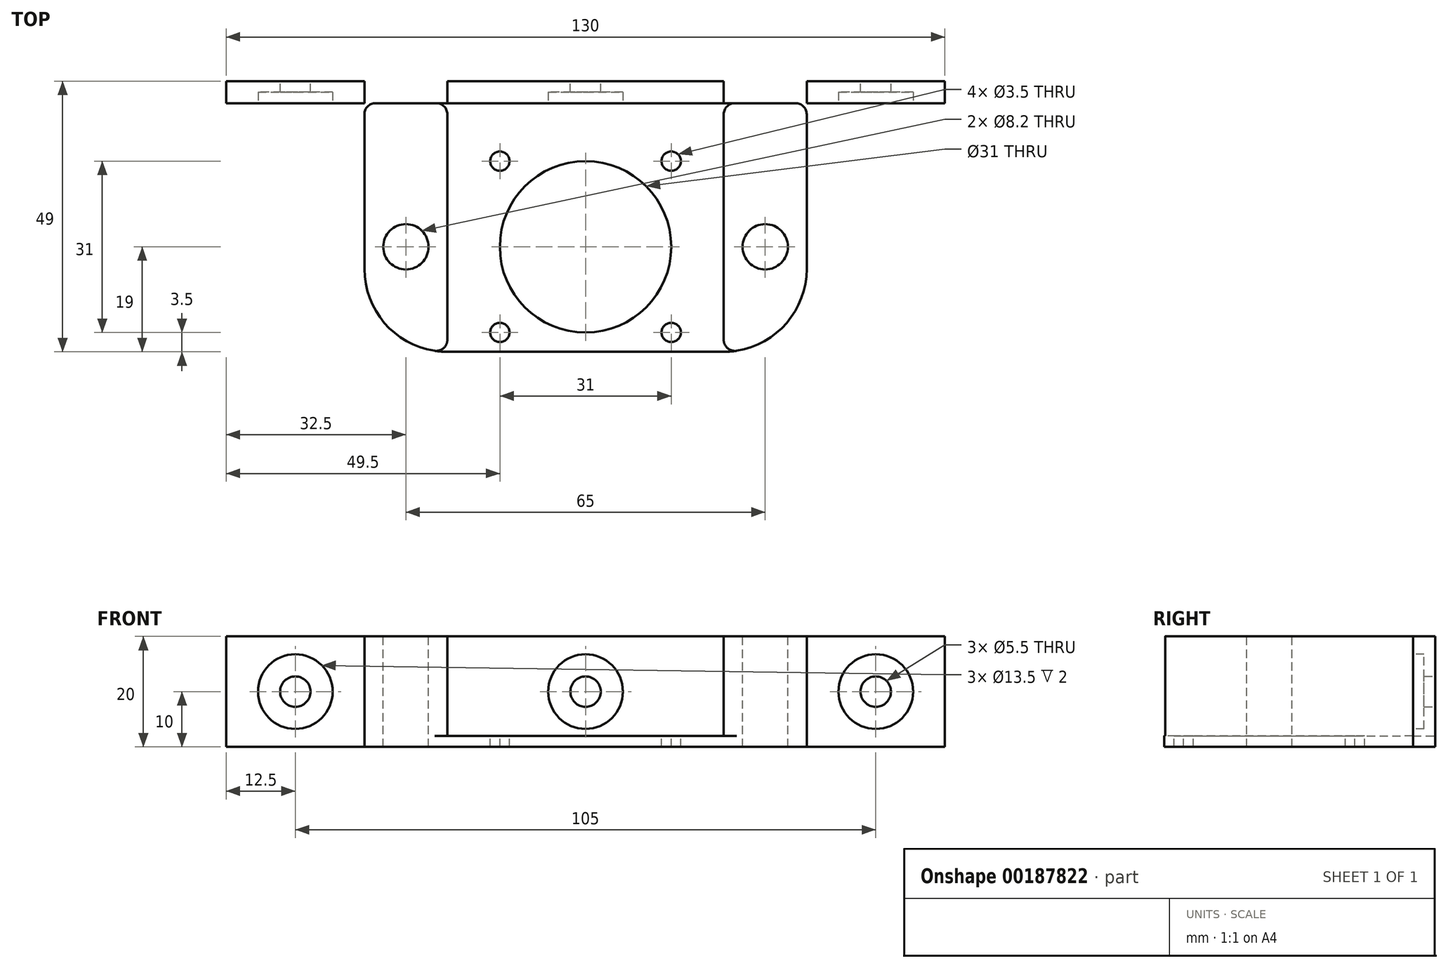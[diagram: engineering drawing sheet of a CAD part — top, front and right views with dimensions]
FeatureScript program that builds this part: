
annotation { "Feature Type Name" : "Feature", "Feature Type Description" : "" }
export const myFeature = defineFeature(function(context is Context, id is Id, definition is map)
    precondition{}
    {
        {
            var Q0;
            Q0=qCreatedBy(makeId("Front.planeOp"),FACE);
            var sketch = newSketch(context, id + "F0", { "sketchPlane" : qUnion([Q0])});
            skLineSegment(sketch, "E0.bottom", {"start": v(0, 0) * mm, "end": v(130, 0) * mm});
            skLineSegment(sketch, "E0.left", {"start": v(0, 0) * mm, "end": v(0, 20) * mm});
            skLineSegment(sketch, "E0.right", {"start": v(130, 0) * mm, "end": v(130, 20) * mm});
            skLineSegment(sketch, "E1.bottom", {"start": v(40, 20) * mm, "end": v(90, 20) * mm});
            skLineSegment(sketch, "E1.top", {"start": v(40, 0) * mm, "end": v(90, 0) * mm});
            skLineSegment(sketch, "E1.left", {"start": v(40, 20) * mm, "end": v(40, 0) * mm});
            skLineSegment(sketch, "E1.right", {"start": v(90, 20) * mm, "end": v(90, 0) * mm});
            skLineSegment(sketch, "E2", {"start": v(0, 20) * mm, "end": v(40, 20) * mm});
            skLineSegment(sketch, "E3", {"start": v(90, 20) * mm, "end": v(130, 20) * mm});
            skLineSegment(sketch, "E4.bottom", {"start": v(40, 20) * mm, "end": v(25, 20) * mm});
            skLineSegment(sketch, "E4.top", {"start": v(40, 0) * mm, "end": v(25, 0) * mm});
            skLineSegment(sketch, "E4.right", {"start": v(25, 20) * mm, "end": v(25, 0) * mm});
            skLineSegment(sketch, "E5.bottom", {"start": v(90, 20) * mm, "end": v(105, 20) * mm});
            skLineSegment(sketch, "E5.top", {"start": v(90, 0) * mm, "end": v(105, 0) * mm});
            skLineSegment(sketch, "E5.right", {"start": v(105, 20) * mm, "end": v(105, 0) * mm});
            skCircle(sketch, "E6", {"center": v(12.5, 10) * mm, "radius": 2.75 * mm});
            skCircle(sketch, "E7", {"center": v(117.5, 10) * mm, "radius": 2.75 * mm});
            skLineSegment(sketch, "E8.top", {"start": v(40, 2) * mm, "end": v(90, 2) * mm});
            skLineSegment(sketch, "E8.left", {"start": v(40, 0) * mm, "end": v(40, 2) * mm});
            skLineSegment(sketch, "E8.right", {"start": v(90, 0) * mm, "end": v(90, 2) * mm});
            skLineSegment(sketch, "E9", {"start": v(0, 10) * mm, "end": v(12.5, 10) * mm});
            skLineSegment(sketch, "E10", {"start": v(12.5, 10) * mm, "end": v(65, 10) * mm});
            skLineSegment(sketch, "E11", {"start": v(117.5, 10) * mm, "end": v(65, 10) * mm});
            skLineSegment(sketch, "E12", {"start": v(117.5, 10) * mm, "end": v(130, 10) * mm});
            skCircle(sketch, "E13", {"center": v(12.5, 10) * mm, "radius": 6.75 * mm});
            skCircle(sketch, "E14", {"center": v(117.5, 10) * mm, "radius": 6.75 * mm});
            skCircle(sketch, "E15", {"center": v(65, 10) * mm, "radius": 2.75 * mm});
            skCircle(sketch, "E16", {"center": v(65.03, 10.1) * mm, "radius": 6.75 * mm});
            skSolve(sketch);
        }
        {
            var Q0;
            {var subQ1=sQuery(id+"F0.wireOp",EDGE,"E0.left");Q0=makeQuery(id+"F0.imprint","IMPRINT",FACE,{"disambiguationData":[TD([[makeQuery(id+"F0.imprint","IMPRINT",EDGE,{"derivedFrom":subQ1}),-1.0]])]});}
            var Q1;
            {var subQ1=sQuery(id+"F0.wireOp",EDGE,"E0.right");Q1=makeQuery(id+"F0.imprint","IMPRINT",FACE,{"disambiguationData":[TD([[makeQuery(id+"F0.imprint","IMPRINT",EDGE,{"derivedFrom":subQ1}),1.0]])]});}
            var Q2;
            Q2=makeQuery(id+"F0.imprint","IMPRINT",FACE,{"disambiguationData":[TD([[makeQuery(id+"F0.imprint","IMPRINT",EDGE,{"derivedFrom":sQuery(id+"F0.wireOp",EDGE,"E1.bottom")}),-1.0]])]});
            var Q3;
            Q3=makeQuery(id+"F0.imprint","IMPRINT",FACE,{"disambiguationData":[TD([[makeQuery(id+"F0.imprint","IMPRINT",EDGE,{"derivedFrom":sQuery(id+"F0.wireOp",EDGE,"E4.bottom")}),1.0]])]});
            var Q4;
            Q4=makeQuery(id+"F0.imprint","IMPRINT",FACE,{"disambiguationData":[TD([[makeQuery(id+"F0.imprint","IMPRINT",EDGE,{"derivedFrom":sQuery(id+"F0.wireOp",EDGE,"E5.bottom")}),-1.0]])]});
            var Q5;
            Q5=makeQuery(id+"F0.imprint","IMPRINT",FACE,{"disambiguationData":[TD([[makeQuery(id+"F0.imprint","IMPRINT",EDGE,{"derivedFrom":sQuery(id+"F0.wireOp",EDGE,"E1.top")}),1.0]])]});
            var Q6;
            {var subQ6=sQuery(id+"F0.wireOp",EDGE,"E4.top");Q6=makeQuery(id+"F0.imprint","IMPRINT",FACE,{"disambiguationData":[TD([[makeQuery(id+"F0.imprint","IMPRINT",EDGE,{"derivedFrom":subQ6}),-1.0]])]});}
            var Q7;
            {var subQ9=sQuery(id+"F0.wireOp",EDGE,"E8.top");Q7=makeQuery(id+"F0.imprint","IMPRINT",FACE,{"disambiguationData":[TD([[makeQuery(id+"F0.imprint","IMPRINT",EDGE,{"derivedFrom":subQ9}),1.0]])]});}
            var Q8;
            {var subQ6=sQuery(id+"F0.wireOp",EDGE,"E5.top");Q8=makeQuery(id+"F0.imprint","IMPRINT",FACE,{"disambiguationData":[TD([[makeQuery(id+"F0.imprint","IMPRINT",EDGE,{"derivedFrom":subQ6}),1.0]])]});}
            var Q9;
            {var subQ3=sQuery(id+"F0.wireOp",EDGE,"E9");var subQ5=sQuery(id+"F0.wireOp",EDGE,"E6");var subQ7=makeQuery(id+"F0.imprint","INTERSECT",VERTEX,{"derivedFrom":[subQ5,subQ3]});Q9=makeQuery(id+"F0.imprint","IMPRINT",FACE,{"disambiguationData":[TD([[makeQuery(id+"F0.imprint","IMPRINT",EDGE,{"disambiguationData":[TD([[subQ7,1.0]])],"derivedFrom":subQ5}),-1.0]])]});}
            var Q10;
            {var subQ3=sQuery(id+"F0.wireOp",EDGE,"E9");var subQ5=sQuery(id+"F0.wireOp",EDGE,"E6");var subQ7=makeQuery(id+"F0.imprint","INTERSECT",VERTEX,{"derivedFrom":[subQ5,subQ3]});Q10=makeQuery(id+"F0.imprint","IMPRINT",FACE,{"disambiguationData":[TD([[makeQuery(id+"F0.imprint","IMPRINT",EDGE,{"disambiguationData":[TD([[subQ7,-1.0]])],"derivedFrom":subQ5}),-1.0]])]});}
            var Q11;
            {var subQ0=sQuery(id+"F0.wireOp",EDGE,"E16");var subQ3=sQuery(id+"F0.wireOp",EDGE,"E10");var subQ4=makeQuery(id+"F0.imprint","INTERSECT",VERTEX,{"derivedFrom":[subQ3,subQ0]});Q11=makeQuery(id+"F0.imprint","IMPRINT",FACE,{"disambiguationData":[TD([[makeQuery(id+"F0.imprint","IMPRINT",EDGE,{"disambiguationData":[TD([[subQ4,-1.0]])],"derivedFrom":subQ3}),-1.0]])]});}
            var Q12;
            {var subQ0=sQuery(id+"F0.wireOp",EDGE,"E16");var subQ3=sQuery(id+"F0.wireOp",EDGE,"E10");var subQ4=makeQuery(id+"F0.imprint","INTERSECT",VERTEX,{"derivedFrom":[subQ3,subQ0]});Q12=makeQuery(id+"F0.imprint","IMPRINT",FACE,{"disambiguationData":[TD([[makeQuery(id+"F0.imprint","IMPRINT",EDGE,{"disambiguationData":[TD([[subQ4,-1.0]])],"derivedFrom":subQ3}),1.0]])]});}
            var Q13;
            {var subQ3=sQuery(id+"F0.wireOp",EDGE,"E11");var subQ5=sQuery(id+"F0.wireOp",EDGE,"E7");var subQ7=makeQuery(id+"F0.imprint","INTERSECT",VERTEX,{"derivedFrom":[subQ5,subQ3]});Q13=makeQuery(id+"F0.imprint","IMPRINT",FACE,{"disambiguationData":[TD([[makeQuery(id+"F0.imprint","IMPRINT",EDGE,{"disambiguationData":[TD([[subQ7,1.0]])],"derivedFrom":subQ5}),-1.0]])]});}
            var Q14;
            {var subQ3=sQuery(id+"F0.wireOp",EDGE,"E11");var subQ5=sQuery(id+"F0.wireOp",EDGE,"E7");var subQ7=makeQuery(id+"F0.imprint","INTERSECT",VERTEX,{"derivedFrom":[subQ5,subQ3]});Q14=makeQuery(id+"F0.imprint","IMPRINT",FACE,{"disambiguationData":[TD([[makeQuery(id+"F0.imprint","IMPRINT",EDGE,{"disambiguationData":[TD([[subQ7,-1.0]])],"derivedFrom":subQ5}),-1.0]])]});}
            extrude(context, id + "F1", {"entities" : qUnion([Q0, Q1, Q2, Q3, Q4, Q5, Q6, Q7, Q8, Q9, Q10, Q11, Q12, Q13, Q14]), "depth" : 4 * mm});
        }
        {
            var Q0;
            Q0=makeQuery(id+"F1.opExtrude","CAP_FACE",FACE,{"disambiguationData":[OSD([sQuery(id+"F0.wireOp",EDGE,"E0.bottom"),sQuery(id+"F0.wireOp",EDGE,"E0.left"),sQuery(id+"F0.wireOp",EDGE,"E0.right"),sQuery(id+"F0.wireOp",EDGE,"E1.bottom"),sQuery(id+"F0.wireOp",EDGE,"E2"),sQuery(id+"F0.wireOp",EDGE,"E3"),sQuery(id+"F0.wireOp",EDGE,"E4.bottom"),sQuery(id+"F0.wireOp",EDGE,"E4.top"),sQuery(id+"F0.wireOp",EDGE,"E5.bottom"),sQuery(id+"F0.wireOp",EDGE,"E5.top"),sQuery(id+"F0.wireOp",EDGE,"E6"),sQuery(id+"F0.wireOp",EDGE,"E7"),sQuery(id+"F0.wireOp",EDGE,"E1.top"),sQuery(id+"F0.wireOp",EDGE,"E15")])],"isStart":false});
            var sketch = newSketch(context, id + "F2", { "sketchPlane" : qUnion([Q0])});
            skCircle(sketch, "E17", {"center": v(12.5, 10) * mm, "radius": 6.75 * mm});
            skCircle(sketch, "E18", {"center": v(65, 10) * mm, "radius": 6.75 * mm});
            skCircle(sketch, "E19", {"center": v(117.5, 10) * mm, "radius": 6.75 * mm});
            skSolve(sketch);
        }
        {
            var Q0;
            Q0=qSketchRegion(id+"F2",true);
            extrude(context, id + "F3", {"entities" : qUnion([Q0]), "operationType" : NewBodyOperationType.REMOVE, "oppositeDirection" : true, "depth" : 2 * mm});
        }
        {
            var Q0;
            Q0=makeQuery(id+"F1.opExtrude","CAP_FACE",FACE,{"disambiguationData":[OSD([sQuery(id+"F0.wireOp",EDGE,"E0.bottom"),sQuery(id+"F0.wireOp",EDGE,"E0.left"),sQuery(id+"F0.wireOp",EDGE,"E0.right"),sQuery(id+"F0.wireOp",EDGE,"E1.bottom"),sQuery(id+"F0.wireOp",EDGE,"E2"),sQuery(id+"F0.wireOp",EDGE,"E3"),sQuery(id+"F0.wireOp",EDGE,"E4.bottom"),sQuery(id+"F0.wireOp",EDGE,"E4.top"),sQuery(id+"F0.wireOp",EDGE,"E5.bottom"),sQuery(id+"F0.wireOp",EDGE,"E5.top"),sQuery(id+"F0.wireOp",EDGE,"E6"),sQuery(id+"F0.wireOp",EDGE,"E7"),sQuery(id+"F0.wireOp",EDGE,"E1.top")])],"isStart":false});
            var sketch = newSketch(context, id + "F4", { "sketchPlane" : qUnion([Q0])});
            skLineSegment(sketch, "E20.bottom", {"start": v(25, 20) * mm, "end": v(40, 20) * mm});
            skLineSegment(sketch, "E20.top", {"start": v(25, 0) * mm, "end": v(40, 0) * mm});
            skLineSegment(sketch, "E20.left", {"start": v(25, 20) * mm, "end": v(25, 0) * mm});
            skLineSegment(sketch, "E20.right", {"start": v(40, 20) * mm, "end": v(40, 0) * mm});
            skLineSegment(sketch, "E21.bottom", {"start": v(90, 20) * mm, "end": v(105, 20) * mm});
            skLineSegment(sketch, "E21.top", {"start": v(90, 0) * mm, "end": v(105, 0) * mm});
            skLineSegment(sketch, "E21.left", {"start": v(90, 20) * mm, "end": v(90, 0) * mm});
            skLineSegment(sketch, "E21.right", {"start": v(105, 20) * mm, "end": v(105, 0) * mm});
            skLineSegment(sketch, "E22", {"start": v(0, 20) * mm, "end": v(25, 20) * mm});
            skLineSegment(sketch, "E23", {"start": v(105, 20) * mm, "end": v(130, 20) * mm});
            skLineSegment(sketch, "E24.bottom", {"start": v(40, 0) * mm, "end": v(90, 0) * mm});
            skLineSegment(sketch, "E24.top", {"start": v(40, 0) * mm, "end": v(90, 0) * mm});
            skLineSegment(sketch, "E24.left", {"start": v(40, 0) * mm, "end": v(40, 0) * mm});
            skLineSegment(sketch, "E24.right", {"start": v(90, 0) * mm, "end": v(90, 0) * mm});
            skLineSegment(sketch, "E25.bottom", {"start": v(90, 0) * mm, "end": v(40, 0) * mm});
            skLineSegment(sketch, "E25.top", {"start": v(90, 2) * mm, "end": v(40, 2) * mm});
            skLineSegment(sketch, "E25.left", {"start": v(90, 0) * mm, "end": v(90, 2) * mm});
            skLineSegment(sketch, "E25.right", {"start": v(40, 0) * mm, "end": v(40, 2) * mm});
            skSolve(sketch);
        }
        {
            var Q0;
            Q0=qSketchRegion(id+"F4",true);
            extrude(context, id + "F5", {"entities" : qUnion([Q0]), "operationType" : NewBodyOperationType.ADD, "depth" : 45 * mm});
        }
        {
            var Q0;
            Q0=makeQuery(id+"F5.opExtrude","SWEPT_FACE",FACE,{"disambiguationData":[OSD([sQuery(id+"F4.wireOp",EDGE,"E25.top")])]});
            var sketch = newSketch(context, id + "F6", { "sketchPlane" : qUnion([Q0])});
            skLineSegment(sketch, "E26.bottom", {"start": v(43.85, -8.85) * mm, "end": v(86.15, -8.85) * mm});
            skLineSegment(sketch, "E26.top", {"start": v(43.85, -51.15) * mm, "end": v(86.15, -51.15) * mm});
            skLineSegment(sketch, "E26.left", {"start": v(43.85, -8.85) * mm, "end": v(43.85, -51.15) * mm});
            skLineSegment(sketch, "E26.right", {"start": v(86.15, -8.85) * mm, "end": v(86.15, -51.15) * mm});
            skLineSegment(sketch, "E27.bottom", {"start": v(49.5, -14.5) * mm, "end": v(80.5, -14.5) * mm});
            skLineSegment(sketch, "E27.top", {"start": v(49.5, -45.5) * mm, "end": v(80.5, -45.5) * mm});
            skLineSegment(sketch, "E27.left", {"start": v(49.5, -14.5) * mm, "end": v(49.5, -45.5) * mm});
            skLineSegment(sketch, "E27.right", {"start": v(80.5, -14.5) * mm, "end": v(80.5, -45.5) * mm});
            skLineSegment(sketch, "E28", {"start": v(43.85, -51.15) * mm, "end": v(49.5, -45.5) * mm});
            skLineSegment(sketch, "E29", {"start": v(80.5, -14.5) * mm, "end": v(86.15, -8.85) * mm});
            skCircle(sketch, "E30", {"center": v(49.5, -14.5) * mm, "radius": 1.75 * mm});
            skCircle(sketch, "E31", {"center": v(49.5, -45.5) * mm, "radius": 1.75 * mm});
            skCircle(sketch, "E32", {"center": v(80.5, -45.5) * mm, "radius": 1.75 * mm});
            skCircle(sketch, "E33", {"center": v(80.5, -14.5) * mm, "radius": 1.75 * mm});
            skLineSegment(sketch, "E34", {"start": v(65, -30) * mm, "end": v(65, 0) * mm});
            skLineSegment(sketch, "E35", {"start": v(43.85, -51.15) * mm, "end": v(40, -51.15) * mm});
            skLineSegment(sketch, "E36", {"start": v(86.15, -51.15) * mm, "end": v(90, -51.15) * mm});
            skLineSegment(sketch, "E37", {"start": v(49.5, -45.5) * mm, "end": v(65, -30) * mm});
            skLineSegment(sketch, "E38", {"start": v(65, -30) * mm, "end": v(80.5, -14.5) * mm});
            skCircle(sketch, "E39", {"center": v(65, -30) * mm, "radius": 15.5 * mm});
            skSolve(sketch);
        }
        {
            var Q0;
            {var subQ0=sQuery(id+"F6.wireOp",EDGE,"E31");var subQ3=sQuery(id+"F6.wireOp",EDGE,"E27.top");var subQ4=makeQuery(id+"F6.imprint","INTERSECT",VERTEX,{"derivedFrom":[subQ3,subQ0]});Q0=makeQuery(id+"F6.imprint","IMPRINT",FACE,{"disambiguationData":[TD([[makeQuery(id+"F6.imprint","IMPRINT",EDGE,{"disambiguationData":[TD([[subQ4,1.0]])],"derivedFrom":subQ0}),1.0]])]});}
            var Q1;
            {var subQ0=sQuery(id+"F6.wireOp",EDGE,"E31");var subQ3=sQuery(id+"F6.wireOp",EDGE,"E27.left");var subQ4=makeQuery(id+"F6.imprint","INTERSECT",VERTEX,{"derivedFrom":[subQ3,subQ0]});Q1=makeQuery(id+"F6.imprint","IMPRINT",FACE,{"disambiguationData":[TD([[makeQuery(id+"F6.imprint","IMPRINT",EDGE,{"disambiguationData":[TD([[subQ4,-1.0]])],"derivedFrom":subQ0}),1.0]])]});}
            var Q2;
            {var subQ1=sQuery(id+"F6.wireOp",EDGE,"E27.left");var subQ3=sQuery(id+"F6.wireOp",EDGE,"E27.bottom");var subQ5=makeQuery(id+"F6.imprint","INTERSECT",VERTEX,{"derivedFrom":[subQ3,subQ1]});Q2=makeQuery(id+"F6.imprint","IMPRINT",FACE,{"disambiguationData":[TD([[makeQuery(id+"F6.imprint","IMPRINT",EDGE,{"disambiguationData":[TD([[subQ5,-1.0]])],"derivedFrom":subQ3}),-1.0]])]});}
            var Q3;
            {var subQ1=sQuery(id+"F6.wireOp",EDGE,"E27.left");var subQ3=sQuery(id+"F6.wireOp",EDGE,"E27.bottom");var subQ5=makeQuery(id+"F6.imprint","INTERSECT",VERTEX,{"derivedFrom":[subQ3,subQ1]});Q3=makeQuery(id+"F6.imprint","IMPRINT",FACE,{"disambiguationData":[TD([[makeQuery(id+"F6.imprint","IMPRINT",EDGE,{"disambiguationData":[TD([[subQ5,-1.0]])],"derivedFrom":subQ3}),1.0]])]});}
            var Q4;
            {var subQ0=sQuery(id+"F6.wireOp",EDGE,"E33");var subQ3=sQuery(id+"F6.wireOp",EDGE,"E27.bottom");var subQ4=makeQuery(id+"F6.imprint","INTERSECT",VERTEX,{"derivedFrom":[subQ3,subQ0]});Q4=makeQuery(id+"F6.imprint","IMPRINT",FACE,{"disambiguationData":[TD([[makeQuery(id+"F6.imprint","IMPRINT",EDGE,{"disambiguationData":[TD([[subQ4,1.0]])],"derivedFrom":subQ0}),1.0]])]});}
            var Q5;
            {var subQ0=sQuery(id+"F6.wireOp",EDGE,"E33");var subQ3=sQuery(id+"F6.wireOp",EDGE,"E27.bottom");var subQ4=makeQuery(id+"F6.imprint","INTERSECT",VERTEX,{"derivedFrom":[subQ3,subQ0]});Q5=makeQuery(id+"F6.imprint","IMPRINT",FACE,{"disambiguationData":[TD([[makeQuery(id+"F6.imprint","IMPRINT",EDGE,{"disambiguationData":[TD([[subQ4,-1.0]])],"derivedFrom":subQ0}),1.0]])]});}
            var Q6;
            {var subQ0=sQuery(id+"F6.wireOp",EDGE,"E33");var subQ3=sQuery(id+"F6.wireOp",EDGE,"E27.right");var subQ4=makeQuery(id+"F6.imprint","INTERSECT",VERTEX,{"derivedFrom":[subQ3,subQ0]});Q6=makeQuery(id+"F6.imprint","IMPRINT",FACE,{"disambiguationData":[TD([[makeQuery(id+"F6.imprint","IMPRINT",EDGE,{"disambiguationData":[TD([[subQ4,-1.0]])],"derivedFrom":subQ0}),1.0]])]});}
            var Q7;
            {var subQ1=sQuery(id+"F6.wireOp",EDGE,"E27.right");var subQ3=sQuery(id+"F6.wireOp",EDGE,"E27.top");var subQ5=makeQuery(id+"F6.imprint","INTERSECT",VERTEX,{"derivedFrom":[subQ3,subQ1]});Q7=makeQuery(id+"F6.imprint","IMPRINT",FACE,{"disambiguationData":[TD([[makeQuery(id+"F6.imprint","IMPRINT",EDGE,{"disambiguationData":[TD([[subQ5,1.0]])],"derivedFrom":subQ3}),-1.0]])]});}
            var Q8;
            {var subQ1=sQuery(id+"F6.wireOp",EDGE,"E27.right");var subQ3=sQuery(id+"F6.wireOp",EDGE,"E27.top");var subQ5=makeQuery(id+"F6.imprint","INTERSECT",VERTEX,{"derivedFrom":[subQ3,subQ1]});Q8=makeQuery(id+"F6.imprint","IMPRINT",FACE,{"disambiguationData":[TD([[makeQuery(id+"F6.imprint","IMPRINT",EDGE,{"disambiguationData":[TD([[subQ5,1.0]])],"derivedFrom":subQ3}),1.0]])]});}
            var Q9;
            {var subQ1=sQuery(id+"F6.wireOp",EDGE,"E33");var subQ3=sQuery(id+"F6.wireOp",EDGE,"E27.right");var subQ5=makeQuery(id+"F6.imprint","INTERSECT",VERTEX,{"derivedFrom":[subQ3,subQ1]});Q9=makeQuery(id+"F6.imprint","IMPRINT",FACE,{"disambiguationData":[TD([[makeQuery(id+"F6.imprint","IMPRINT",EDGE,{"disambiguationData":[TD([[subQ5,1.0]])],"derivedFrom":subQ1}),1.0]])]});}
            var Q10;
            {var subQ1=sQuery(id+"F6.wireOp",EDGE,"E31");var subQ3=sQuery(id+"F6.wireOp",EDGE,"E27.top");var subQ5=makeQuery(id+"F6.imprint","INTERSECT",VERTEX,{"derivedFrom":[subQ3,subQ1]});Q10=makeQuery(id+"F6.imprint","IMPRINT",FACE,{"disambiguationData":[TD([[makeQuery(id+"F6.imprint","IMPRINT",EDGE,{"disambiguationData":[TD([[subQ5,-1.0]])],"derivedFrom":subQ1}),1.0]])]});}
            var Q11;
            {var subQ1=sQuery(id+"F6.wireOp",EDGE,"E31");var subQ3=sQuery(id+"F6.wireOp",EDGE,"E27.left");var subQ5=makeQuery(id+"F6.imprint","INTERSECT",VERTEX,{"derivedFrom":[subQ3,subQ1]});Q11=makeQuery(id+"F6.imprint","IMPRINT",FACE,{"disambiguationData":[TD([[makeQuery(id+"F6.imprint","IMPRINT",EDGE,{"disambiguationData":[TD([[subQ5,1.0]])],"derivedFrom":subQ1}),1.0]])]});}
            var Q12;
            {var subQ0=sQuery(id+"F6.wireOp",EDGE,"E39");var subQ3=sQuery(id+"F6.wireOp",EDGE,"E34");var subQ4=makeQuery(id+"F6.imprint","INTERSECT",VERTEX,{"derivedFrom":[subQ3,subQ0]});Q12=makeQuery(id+"F6.imprint","IMPRINT",FACE,{"disambiguationData":[TD([[makeQuery(id+"F6.imprint","IMPRINT",EDGE,{"disambiguationData":[TD([[subQ4,-1.0]])],"derivedFrom":subQ0}),1.0]])]});}
            var Q13;
            {var subQ0=sQuery(id+"F6.wireOp",EDGE,"E39");var subQ3=sQuery(id+"F6.wireOp",EDGE,"E34");var subQ4=makeQuery(id+"F6.imprint","INTERSECT",VERTEX,{"derivedFrom":[subQ3,subQ0]});Q13=makeQuery(id+"F6.imprint","IMPRINT",FACE,{"disambiguationData":[TD([[makeQuery(id+"F6.imprint","IMPRINT",EDGE,{"disambiguationData":[TD([[subQ4,1.0]])],"derivedFrom":subQ0}),1.0]])]});}
            var Q14;
            {var subQ0=sQuery(id+"F6.wireOp",EDGE,"E39");var subQ3=sQuery(id+"F6.wireOp",EDGE,"E37");var subQ4=makeQuery(id+"F6.imprint","INTERSECT",VERTEX,{"derivedFrom":[subQ3,subQ0]});Q14=makeQuery(id+"F6.imprint","IMPRINT",FACE,{"disambiguationData":[TD([[makeQuery(id+"F6.imprint","IMPRINT",EDGE,{"disambiguationData":[TD([[subQ4,-1.0]])],"derivedFrom":subQ0}),1.0]])]});}
            extrude(context, id + "F7", {"entities" : qUnion([Q0, Q1, Q2, Q3, Q4, Q5, Q6, Q7, Q8, Q9, Q10, Q11, Q12, Q13, Q14]), "operationType" : NewBodyOperationType.REMOVE, "oppositeDirection" : true, "depth" : 2 * mm});
        }
        {
            var Q0;
            Q0=makeQuery(id+"F5.boolean.opBoolean","MERGE",FACE,{"derivedFrom":[makeQuery(id+"F1.opExtrude","SWEPT_FACE",FACE,{"disambiguationData":[OSD([sQuery(id+"F0.wireOp",EDGE,"E1.bottom"),sQuery(id+"F0.wireOp",EDGE,"E2"),sQuery(id+"F0.wireOp",EDGE,"E3"),sQuery(id+"F0.wireOp",EDGE,"E4.bottom"),sQuery(id+"F0.wireOp",EDGE,"E5.bottom")])]}),makeQuery(id+"F5.opExtrude","SWEPT_FACE",FACE,{"disambiguationData":[OSD([sQuery(id+"F4.wireOp",EDGE,"E20.bottom")])]}),makeQuery(id+"F5.opExtrude","SWEPT_FACE",FACE,{"disambiguationData":[OSD([sQuery(id+"F4.wireOp",EDGE,"E21.bottom")])]})]});
            var sketch = newSketch(context, id + "F8", { "sketchPlane" : qUnion([Q0])});
            skCircle(sketch, "E40", {"center": v(32.5, -30) * mm, "radius": 4.1 * mm});
            skCircle(sketch, "E41", {"center": v(97.5, -30) * mm, "radius": 4.1 * mm});
            skLineSegment(sketch, "E42", {"start": v(32.5, -30) * mm, "end": v(32.5, 0) * mm});
            skLineSegment(sketch, "E43", {"start": v(97.5, -30) * mm, "end": v(97.5, 0) * mm});
            skLineSegment(sketch, "E44", {"start": v(32.5, -30) * mm, "end": v(97.5, -30) * mm});
            skLineSegment(sketch, "E45", {"start": v(32.5, 0) * mm, "end": v(0, 0) * mm});
            skLineSegment(sketch, "E46", {"start": v(97.5, 0) * mm, "end": v(130, 0) * mm});
            skSolve(sketch);
        }
        {
            var Q0;
            {var subQ1=sQuery(id+"F8.wireOp",EDGE,"E40");var subQ3=sQuery(id+"F8.wireOp",EDGE,"E42");var subQ5=makeQuery(id+"F8.imprint","INTERSECT",VERTEX,{"derivedFrom":[subQ1,subQ3]});Q0=makeQuery(id+"F8.imprint","IMPRINT",FACE,{"disambiguationData":[TD([[makeQuery(id+"F8.imprint","IMPRINT",EDGE,{"disambiguationData":[TD([[subQ5,-1.0]])],"derivedFrom":subQ1}),1.0]])]});}
            var Q1;
            {var subQ1=sQuery(id+"F8.wireOp",EDGE,"E40");var subQ3=sQuery(id+"F8.wireOp",EDGE,"E42");var subQ5=makeQuery(id+"F8.imprint","INTERSECT",VERTEX,{"derivedFrom":[subQ1,subQ3]});Q1=makeQuery(id+"F8.imprint","IMPRINT",FACE,{"disambiguationData":[TD([[makeQuery(id+"F8.imprint","IMPRINT",EDGE,{"disambiguationData":[TD([[subQ5,1.0]])],"derivedFrom":subQ1}),1.0]])]});}
            var Q2;
            {var subQ1=sQuery(id+"F8.wireOp",EDGE,"E41");var subQ3=sQuery(id+"F8.wireOp",EDGE,"E43");var subQ5=makeQuery(id+"F8.imprint","INTERSECT",VERTEX,{"derivedFrom":[subQ1,subQ3]});Q2=makeQuery(id+"F8.imprint","IMPRINT",FACE,{"disambiguationData":[TD([[makeQuery(id+"F8.imprint","IMPRINT",EDGE,{"disambiguationData":[TD([[subQ5,-1.0]])],"derivedFrom":subQ1}),1.0]])]});}
            var Q3;
            {var subQ1=sQuery(id+"F8.wireOp",EDGE,"E41");var subQ3=sQuery(id+"F8.wireOp",EDGE,"E43");var subQ5=makeQuery(id+"F8.imprint","INTERSECT",VERTEX,{"derivedFrom":[subQ1,subQ3]});Q3=makeQuery(id+"F8.imprint","IMPRINT",FACE,{"disambiguationData":[TD([[makeQuery(id+"F8.imprint","IMPRINT",EDGE,{"disambiguationData":[TD([[subQ5,1.0]])],"derivedFrom":subQ1}),1.0]])]});}
            extrude(context, id + "F9", {"entities" : qUnion([Q0, Q1, Q2, Q3]), "operationType" : NewBodyOperationType.REMOVE, "oppositeDirection" : true, "depth" : 20 * mm});
        }
        {
            var Q0;
            Q0=makeQuery(id+"F5.opExtrude","CAP_EDGE",EDGE,{"disambiguationData":[OSD([sQuery(id+"F4.wireOp",EDGE,"E20.left")])],"isStart":true});
            var Q1;
            Q1=makeQuery(id+"F5.opExtrude","CAP_EDGE",EDGE,{"disambiguationData":[OSD([sQuery(id+"F4.wireOp",EDGE,"E21.right")])],"isStart":true});
            var Q2;
            Q2=makeQuery(id+"F5.opExtrude","CAP_EDGE",EDGE,{"disambiguationData":[OSD([sQuery(id+"F4.wireOp",EDGE,"E20.right")])],"isStart":true});
            var Q3;
            Q3=makeQuery(id+"F5.opExtrude","CAP_EDGE",EDGE,{"disambiguationData":[OSD([sQuery(id+"F4.wireOp",EDGE,"E21.left")])],"isStart":true});
            fillet(context, id + "F10", {"entities" : qUnion([Q0, Q1, Q2, Q3]), "radius" : 2 * mm, "tangentPropagation" : true, "allowEdgeOverflow" : false});
        }
        {
            var Q0;
            Q0=makeQuery(id+"F5.opExtrude","CAP_EDGE",EDGE,{"disambiguationData":[OSD([sQuery(id+"F4.wireOp",EDGE,"E21.right")])],"isStart":false});
            var Q1;
            Q1=makeQuery(id+"F5.opExtrude","CAP_EDGE",EDGE,{"disambiguationData":[OSD([sQuery(id+"F4.wireOp",EDGE,"E20.left")])],"isStart":false});
            fillet(context, id + "F11", {"entities" : qUnion([Q0, Q1]), "radius" : 15 * mm, "allowEdgeOverflow" : false});
        }
        {
            var Q0;
            Q0=makeQuery(id+"F11.opFillet","BLEND_EDGE",EDGE,{"blendedFrom":[makeQuery(id+"F5.opExtrude","CAP_EDGE",EDGE,{"disambiguationData":[OSD([sQuery(id+"F4.wireOp",EDGE,"E20.left")])],"isStart":false}),makeQuery(id+"F5.opExtrude","SWEPT_FACE",FACE,{"disambiguationData":[OSD([sQuery(id+"F4.wireOp",EDGE,"E20.right")])]})],"blendedInto":[makeQuery(id+"F5.opExtrude","SWEPT_FACE",FACE,{"disambiguationData":[OSD([sQuery(id+"F4.wireOp",EDGE,"E20.right")])]})]});
            var Q1;
            Q1=makeQuery(id+"F11.opFillet","BLEND_EDGE",EDGE,{"blendedFrom":[makeQuery(id+"F5.opExtrude","CAP_EDGE",EDGE,{"disambiguationData":[OSD([sQuery(id+"F4.wireOp",EDGE,"E21.right")])],"isStart":false}),makeQuery(id+"F5.opExtrude","SWEPT_FACE",FACE,{"disambiguationData":[OSD([sQuery(id+"F4.wireOp",EDGE,"E21.left")])]})],"blendedInto":[makeQuery(id+"F5.opExtrude","SWEPT_FACE",FACE,{"disambiguationData":[OSD([sQuery(id+"F4.wireOp",EDGE,"E21.left")])]})]});
            fillet(context, id + "F12", {"entities" : qUnion([Q0, Q1]), "radius" : 2 * mm, "tangentPropagation" : true, "allowEdgeOverflow" : false});
        }
    });
